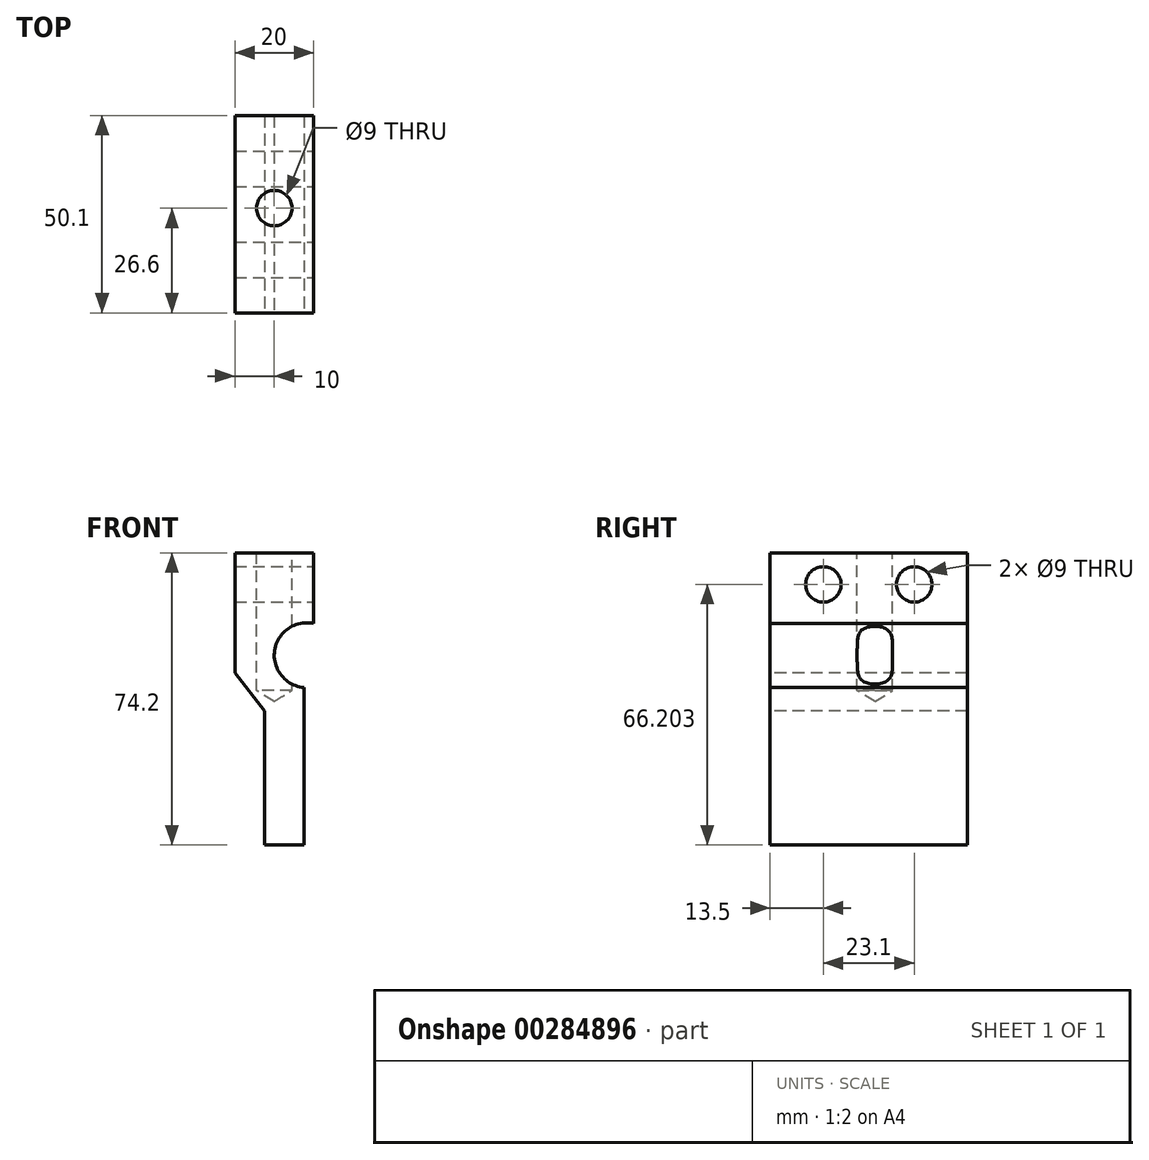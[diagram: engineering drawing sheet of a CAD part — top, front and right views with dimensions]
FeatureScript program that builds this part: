
annotation { "Feature Type Name" : "Feature", "Feature Type Description" : "" }
export const myFeature = defineFeature(function(context is Context, id is Id, definition is map)
    precondition{}
    {
        {
            var Q0;
            Q0=qCreatedBy(makeId("Front.planeOp"),FACE);
            var sketch = newSketch(context, id + "F0", { "sketchPlane" : qUnion([Q0])});
            skLineSegment(sketch, "E0", {"start": v(0, 38.12) * mm, "end": v(-20, 38.12) * mm});
            skLineSegment(sketch, "E1", {"start": v(0, 38.12) * mm, "end": v(0, 19.82) * mm});
            skLineSegment(sketch, "E2", {"start": v(-20, 38.12) * mm, "end": v(-20, 7.62) * mm});
            skLineSegment(sketch, "E3", {"start": v(-20, 7.62) * mm, "end": v(-12.4, -1.98) * mm});
            skLineSegment(sketch, "E4", {"start": v(-12.4, -1.98) * mm, "end": v(-12.4, -36.08) * mm});
            skLineSegment(sketch, "E5", {"start": v(-12.4, -36.08) * mm, "end": v(-2.4, -36.08) * mm});
            skLineSegment(sketch, "E6", {"start": v(-2.4, -36.08) * mm, "end": v(-2.4, 3.92) * mm});
            skArc(sketch, "E7", {"start": v(1.21, 19.82) * mm, "mid": v(-9.8, 13.96) * mm, "end": v(-2.4, 3.92) * mm});
            skSolve(sketch);
        }
        {
            var Q0;
            {var subQ1=sQuery(id+"F0.wireOp",EDGE,"E0");Q0=makeQuery(id+"F0.imprint","IMPRINT",FACE,{"disambiguationData":[TD([[makeQuery(id+"F0.imprint","IMPRINT",EDGE,{"derivedFrom":subQ1}),1.0]])]});}
            extrude(context, id + "F1", {"entities" : qUnion([Q0]), "oppositeDirection" : true, "depth" : 50.1 * mm, "offsetDistance" : 25.4 * mm});
        }
        {
            var Q0;
            Q0=makeQuery(id+"F1.opExtrude","SWEPT_FACE",FACE,{"disambiguationData":[OSD([sQuery(id+"F0.wireOp",EDGE,"E1")])]});
            var sketch = newSketch(context, id + "F2", { "sketchPlane" : qUnion([Q0])});
            skPoint(sketch, "E8", {"position": v(13.5, 30.12) * mm});
            skPoint(sketch, "E9", {"position": v(36.6, 30.12) * mm});
            skSolve(sketch);
        }
        {
            var Q0;
            Q0=sQuery(id+"F2.wireOp",VERTEX,"E8");
            var Q1;
            Q1=sQuery(id+"F2.wireOp",VERTEX,"E9");
            var Q2;
            Q2=makeQuery(id+"F1.opExtrude","SWEPT_BODY",BODY,{"disambiguationData":[OSD([sQuery(id+"F0.wireOp",EDGE,"E0"),sQuery(id+"F0.wireOp",EDGE,"E1"),sQuery(id+"F0.wireOp",EDGE,"E2"),sQuery(id+"F0.wireOp",EDGE,"E3"),sQuery(id+"F0.wireOp",EDGE,"E4"),sQuery(id+"F0.wireOp",EDGE,"E5"),sQuery(id+"F0.wireOp",EDGE,"E6"),sQuery(id+"F0.wireOp",EDGE,"E7")])]});
            hole(context, id + "F3", {"style" : HoleStyle.SIMPLE, "endStyle" : HoleEndStyle.THROUGH, "standardTappedOrClearance" : lookupTablePath({ "fit" : "Normal", "standard" : "ISO", "size" : "M8", "type" : "Clearance" }), "standardBlindInLast" : lookupTablePath({ "fit" : "Normal", "standard" : "ISO", "engagement" : "75%", "pitch" : "1.25 mm", "size" : "M8", "type" : "Clearance & tapped" }), "holeDiameter" : 9 * mm, "majorDiameter" : 6.35 * mm, "isTappedThrough" : true, "tappedDepth" : 12.7 * mm, "tapClearance" : 3, "locations" : qUnion([Q0, Q1]), "scope" : qUnion([Q2])});
        }
        {
            var Q0;
            Q0=makeQuery(id+"F1.opExtrude","SWEPT_FACE",FACE,{"disambiguationData":[OSD([sQuery(id+"F0.wireOp",EDGE,"E0")])]});
            var sketch = newSketch(context, id + "F4", { "sketchPlane" : qUnion([Q0])});
            skPoint(sketch, "E10", {"position": v(-10, 26.6) * mm});
            skSolve(sketch);
        }
        {
            var Q0;
            Q0=sQuery(id+"F4.wireOp",VERTEX,"E10");
            var Q1;
            Q1=makeQuery(id+"F1.opExtrude","SWEPT_BODY",BODY,{"disambiguationData":[OSD([sQuery(id+"F0.wireOp",EDGE,"E0"),sQuery(id+"F0.wireOp",EDGE,"E1"),sQuery(id+"F0.wireOp",EDGE,"E2"),sQuery(id+"F0.wireOp",EDGE,"E3"),sQuery(id+"F0.wireOp",EDGE,"E4"),sQuery(id+"F0.wireOp",EDGE,"E5"),sQuery(id+"F0.wireOp",EDGE,"E6"),sQuery(id+"F0.wireOp",EDGE,"E7")])]});
            hole(context, id + "F5", {"style" : HoleStyle.SIMPLE, "endStyle" : HoleEndStyle.BLIND, "standardTappedOrClearance" : lookupTablePath({ "fit" : "Normal", "standard" : "ISO", "size" : "M8", "type" : "Clearance" }), "standardBlindInLast" : lookupTablePath({ "fit" : "Normal", "standard" : "ISO", "engagement" : "75%", "pitch" : "1.25 mm", "size" : "M8", "type" : "Clearance & tapped" }), "holeDiameter" : 9 * mm, "majorDiameter" : 6.35 * mm, "holeDepth" : 35 * mm, "isTappedThrough" : true, "tappedDepth" : 12.7 * mm, "tapClearance" : 3, "locations" : qUnion([Q0]), "scope" : qUnion([Q1])});
        }
    });
